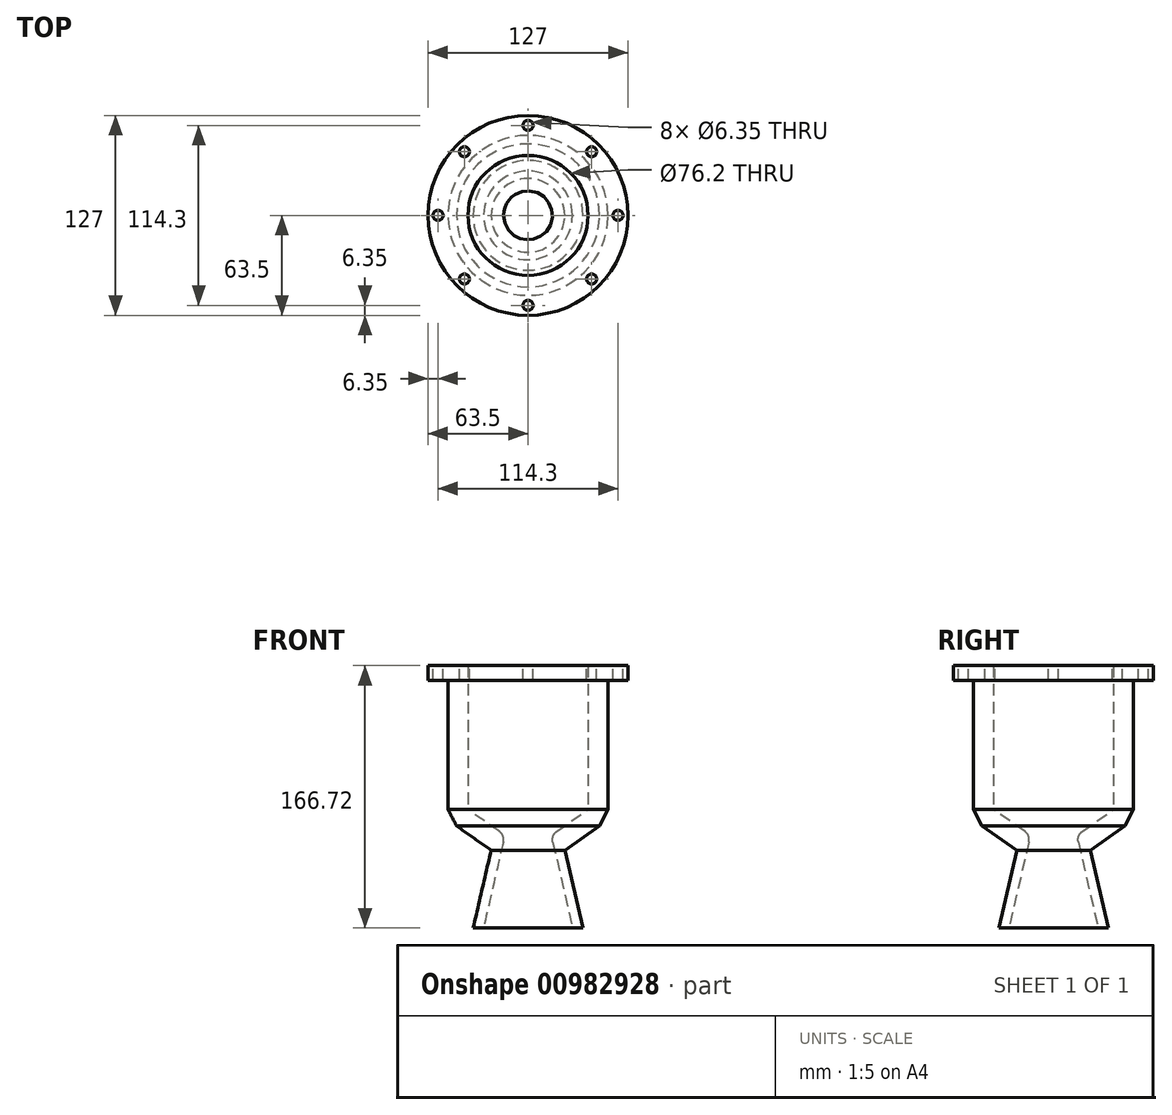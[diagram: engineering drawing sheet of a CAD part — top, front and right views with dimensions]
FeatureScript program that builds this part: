
annotation { "Feature Type Name" : "Feature", "Feature Type Description" : "" }
export const myFeature = defineFeature(function(context is Context, id is Id, definition is map)
    precondition{}
    {
        {
            var Q0;
            Q0=qCreatedBy(makeId("Front.planeOp"),FACE);
            var sketch = newSketch(context, id + "F0", { "sketchPlane" : qUnion([Q0])});
            skLineSegment(sketch, "E0", {"start": v(0, 0) * mm, "end": v(50.8, 0) * mm});
            skLineSegment(sketch, "E1.bottom", {"start": v(50.8, 0) * mm, "end": v(38.1, 0) * mm});
            skLineSegment(sketch, "E1.top", {"start": v(50.8, 91.44) * mm, "end": v(38.1, 91.44) * mm});
            skLineSegment(sketch, "E1.left", {"start": v(50.8, 0) * mm, "end": v(50.8, 91.44) * mm});
            skLineSegment(sketch, "E1.right", {"start": v(38.1, 0) * mm, "end": v(38.1, 91.44) * mm});
            skLineSegment(sketch, "E2.bottom", {"start": v(38.1, 91.44) * mm, "end": v(63.5, 91.44) * mm});
            skLineSegment(sketch, "E2.top", {"start": v(38.1, 81.91) * mm, "end": v(63.5, 81.91) * mm});
            skLineSegment(sketch, "E2.left", {"start": v(38.1, 91.44) * mm, "end": v(38.1, 81.91) * mm});
            skLineSegment(sketch, "E2.right", {"start": v(63.5, 91.44) * mm, "end": v(63.5, 81.92) * mm});
            skLineSegment(sketch, "E3", {"start": v(0, 0) * mm, "end": v(14.73, 0) * mm});
            skLineSegment(sketch, "E4", {"start": v(38.1, 0) * mm, "end": v(18.24, -13.9) * mm});
            skLineSegment(sketch, "E5", {"start": v(38.1, 0) * mm, "end": v(45.38, -10.4) * mm});
            skLineSegment(sketch, "E6", {"start": v(50.8, 0) * mm, "end": v(45.38, -10.4) * mm});
            skLineSegment(sketch, "E7", {"start": v(0, 0) * mm, "end": v(28.2, 0) * mm});
            skLineSegment(sketch, "E8", {"start": v(15.7, -20.54) * mm, "end": v(28.2, -74.67) * mm});
            skLineSegment(sketch, "E9", {"start": v(45.38, -10.4) * mm, "end": v(17.81, -29.7) * mm});
            skLineSegment(sketch, "E10", {"start": v(23.42, -25.78) * mm, "end": v(34.85, -75.28) * mm});
            skLineSegment(sketch, "E11", {"start": v(0, 0) * mm, "end": v(0, 80.76) * mm});
            skLineSegment(sketch, "E12", {"start": v(28.2, -74.67) * mm, "end": v(34.85, -75.28) * mm});
            skPoint(sketch, "E13.visualSharp", {"position": v(14.73, -16.36) * mm});
            skArc(sketch, "E13.filletArc", {"start": v(18.24, -13.9) * mm, "mid": v(15.95, -16.83) * mm, "end": v(15.7, -20.54) * mm});
            skLineSegment(sketch, "E14", {"start": v(0, 0) * mm, "end": v(0, -77.4) * mm});
            skSolve(sketch);
        }
        {
            var Q0;
            Q0=qSketchRegion(id+"F0",true);
            var Q1;
            Q1=sQuery(id+"F0.wireOp",EDGE,"E11");
            revolve(context, id + "F1", {"entities" : qUnion([Q0]), "axis" : qUnion([Q1]), "revolveType" : RevolveType.FULL});
        }
        {
            var Q0;
            Q0=makeQuery(id+"F1.opRevolve","SWEPT_FACE",FACE,{"disambiguationData":[OSD([sQuery(id+"F0.wireOp",EDGE,"E2.bottom")])]});
            var sketch = newSketch(context, id + "F2", { "sketchPlane" : qUnion([Q0])});
            skArc(sketch, "E15", {"start": v(40.41, 40.41) * mm, "mid": v(23.33, 52.17) * mm, "end": v(3.17, 57.06) * mm});
            skCircle(sketch, "E16", {"center": v(0, 57.15) * mm, "radius": 3.18 * mm});
            skCircle(sketch, "E17.1.0", {"center": v(-40.41, 40.41) * mm, "radius": 3.18 * mm});
            skCircle(sketch, "E17.2.0", {"center": v(-57.15, 0) * mm, "radius": 3.18 * mm});
            skCircle(sketch, "E17.3.0", {"center": v(-40.41, -40.41) * mm, "radius": 3.18 * mm});
            skCircle(sketch, "E17.4.0", {"center": v(0, -57.15) * mm, "radius": 3.18 * mm});
            skCircle(sketch, "E17.5.0", {"center": v(40.41, -40.41) * mm, "radius": 3.18 * mm});
            skCircle(sketch, "E17.6.0", {"center": v(57.15, 0) * mm, "radius": 3.18 * mm});
            skCircle(sketch, "E17.7.0", {"center": v(40.41, 40.41) * mm, "radius": 3.18 * mm});
            skArc(sketch, "E18.trimOffspring", {"start": v(57.15, 0) * mm, "mid": v(53.39, 20.4) * mm, "end": v(42.6, 38.1) * mm});
            skArc(sketch, "E19.trimOffspring", {"start": v(40.41, -40.41) * mm, "mid": v(52.17, -23.33) * mm, "end": v(57.06, -3.17) * mm});
            skArc(sketch, "E20.trimOffspring", {"start": v(0, -57.15) * mm, "mid": v(20.4, -53.39) * mm, "end": v(38.1, -42.6) * mm});
            skArc(sketch, "E21.trimOffspring", {"start": v(-40.41, -40.41) * mm, "mid": v(-23.33, -52.17) * mm, "end": v(-3.17, -57.06) * mm});
            skArc(sketch, "E22.trimOffspring", {"start": v(-57.15, 0) * mm, "mid": v(-53.39, -20.4) * mm, "end": v(-42.6, -38.1) * mm});
            skArc(sketch, "E23.trimOffspring", {"start": v(-40.41, 40.41) * mm, "mid": v(-52.17, 23.33) * mm, "end": v(-57.06, 3.17) * mm});
            skArc(sketch, "E24.trimOffspring", {"start": v(0, 57.15) * mm, "mid": v(-20.4, 53.39) * mm, "end": v(-38.1, 42.6) * mm});
            skSolve(sketch);
        }
        {
            var Q0;
            {var subQ0=sQuery(id+"F2.wireOp",EDGE,"E16");var subQ1=makeQuery(id+"F2.imprint","INTERSECT",VERTEX,{"derivedFrom":[sQuery(id+"F2.wireOp",EDGE,"E15"),subQ0]});Q0=makeQuery(id+"F2.imprint","IMPRINT",FACE,{"disambiguationData":[TD([[makeQuery(id+"F2.imprint","IMPRINT",EDGE,{"disambiguationData":[TD([[subQ1,1.0]])],"derivedFrom":subQ0}),1.0]])]});}
            var Q1;
            {var subQ0=sQuery(id+"F2.wireOp",EDGE,"E17.7.0");var subQ1=makeQuery(id+"F2.imprint","INTERSECT",VERTEX,{"derivedFrom":[subQ0,sQuery(id+"F2.wireOp",EDGE,"E18.trimOffspring")]});Q1=makeQuery(id+"F2.imprint","IMPRINT",FACE,{"disambiguationData":[TD([[makeQuery(id+"F2.imprint","IMPRINT",EDGE,{"disambiguationData":[TD([[subQ1,1.0]])],"derivedFrom":subQ0}),1.0]])]});}
            var Q2;
            {var subQ0=sQuery(id+"F2.wireOp",EDGE,"E17.6.0");var subQ1=makeQuery(id+"F2.imprint","INTERSECT",VERTEX,{"derivedFrom":[subQ0,sQuery(id+"F2.wireOp",EDGE,"E19.trimOffspring")]});Q2=makeQuery(id+"F2.imprint","IMPRINT",FACE,{"disambiguationData":[TD([[makeQuery(id+"F2.imprint","IMPRINT",EDGE,{"disambiguationData":[TD([[subQ1,1.0]])],"derivedFrom":subQ0}),1.0]])]});}
            var Q3;
            {var subQ0=sQuery(id+"F2.wireOp",EDGE,"E17.5.0");var subQ1=makeQuery(id+"F2.imprint","INTERSECT",VERTEX,{"derivedFrom":[subQ0,sQuery(id+"F2.wireOp",EDGE,"E20.trimOffspring")]});Q3=makeQuery(id+"F2.imprint","IMPRINT",FACE,{"disambiguationData":[TD([[makeQuery(id+"F2.imprint","IMPRINT",EDGE,{"disambiguationData":[TD([[subQ1,1.0]])],"derivedFrom":subQ0}),1.0]])]});}
            var Q4;
            {var subQ0=sQuery(id+"F2.wireOp",EDGE,"E17.4.0");var subQ1=makeQuery(id+"F2.imprint","INTERSECT",VERTEX,{"derivedFrom":[subQ0,sQuery(id+"F2.wireOp",EDGE,"E21.trimOffspring")]});Q4=makeQuery(id+"F2.imprint","IMPRINT",FACE,{"disambiguationData":[TD([[makeQuery(id+"F2.imprint","IMPRINT",EDGE,{"disambiguationData":[TD([[subQ1,1.0]])],"derivedFrom":subQ0}),1.0]])]});}
            var Q5;
            {var subQ0=sQuery(id+"F2.wireOp",EDGE,"E17.3.0");var subQ1=makeQuery(id+"F2.imprint","INTERSECT",VERTEX,{"derivedFrom":[subQ0,sQuery(id+"F2.wireOp",EDGE,"E22.trimOffspring")]});Q5=makeQuery(id+"F2.imprint","IMPRINT",FACE,{"disambiguationData":[TD([[makeQuery(id+"F2.imprint","IMPRINT",EDGE,{"disambiguationData":[TD([[subQ1,1.0]])],"derivedFrom":subQ0}),1.0]])]});}
            var Q6;
            {var subQ0=sQuery(id+"F2.wireOp",EDGE,"E17.2.0");var subQ1=makeQuery(id+"F2.imprint","INTERSECT",VERTEX,{"derivedFrom":[subQ0,sQuery(id+"F2.wireOp",EDGE,"E23.trimOffspring")]});Q6=makeQuery(id+"F2.imprint","IMPRINT",FACE,{"disambiguationData":[TD([[makeQuery(id+"F2.imprint","IMPRINT",EDGE,{"disambiguationData":[TD([[subQ1,1.0]])],"derivedFrom":subQ0}),1.0]])]});}
            var Q7;
            {var subQ0=sQuery(id+"F2.wireOp",EDGE,"E17.1.0");var subQ1=makeQuery(id+"F2.imprint","INTERSECT",VERTEX,{"derivedFrom":[subQ0,sQuery(id+"F2.wireOp",EDGE,"E24.trimOffspring")]});Q7=makeQuery(id+"F2.imprint","IMPRINT",FACE,{"disambiguationData":[TD([[makeQuery(id+"F2.imprint","IMPRINT",EDGE,{"disambiguationData":[TD([[subQ1,1.0]])],"derivedFrom":subQ0}),1.0]])]});}
            extrude(context, id + "F3", {"entities" : qUnion([Q0, Q1, Q2, Q3, Q4, Q5, Q6, Q7]), "operationType" : NewBodyOperationType.REMOVE, "oppositeDirection" : true, "depth" : 25.4 * mm, "offsetDistance" : 25.4 * mm});
        }
    });
